# Revit family: AnchorPoint_Kattsafe_ConcreteMount
name_source: partatom
category: Specialty Equipment
units: mm (PartAtom-declared; Revit-internal decimal feet)

## family parameters
Cut with Voids When Loaded = Yes
Enable Cutting in Views = No
Host = Face
Maintain Annotation Orientation = No
OmniClass Number = 23.27.71.21
Part Type = Normal
Room Calculation Point = No
Round Connector Dimension = Use Diameter
Shared = No

## types (2) — shared parameters
Assembly Code = E1090100
Description = Kattsafe concrete mount anchors for personnel who use a harness and lanyard fall protection system, when working on a concrete surface. Available in cast-in, low profile and raised designs they are adaptable and easy to install.
ElementType = Fall Protection
Export Type to IFC As = IfcBuildingElementProxy
FixedHoop = Yes
IfcExportAs = IfcBuildingElementProxy
IfcExportType = USERDEFINED
Manufacturer = Kattsafe®
ManufacturerURLProductSpecific = https://kattsafe.com.au
Material = Steel_Stainless_Kattsafe_Satin
ModifiedIssue = 20240430 $
Type IFC Predefined Type = USERDEFINED
URL = https://kattsafe.com.au
Uniclass2015Code = Pr_40_70_75_75
Uniclass2015Title = Safety access anchor devices
Uniclass2015Version = Products v1.23
zero-valued in all types: Default Elevation

## per-type parameters (varying)
| type | ManufacturerOverallDepth | ManufacturerOverallHeight | ManufacturerOverallWidth | ManufacturerSpecCode | Model | Swivel | Type Comments |
| Fixed Hoop (AP125A) | 60 mm  [stored 0.19685 ft] | 164 mm  [stored 0.538058 ft] | 60 mm  [stored 0.19685 ft] | AP125A | AP125A | No | Concrete Mount Anchor - 15kN rated - 0.3kg |
| Swivel (AP125S) | 105 mm  [stored 0.344488 ft] | 145 mm  [stored 0.475722 ft] | 105 mm  [stored 0.344488 ft] | AP125S | AP125S | Yes | Concrete Mount Swivel Anchor - 15kN rated - 0.5kg |

note: [stored X ft] marks values corroborated as IEEE doubles in the binary element streams (Revit-internal decimal feet)

## geometry (parser evidence)
native form markers: Sweep x3
no freeform markers — native parametric forms only
